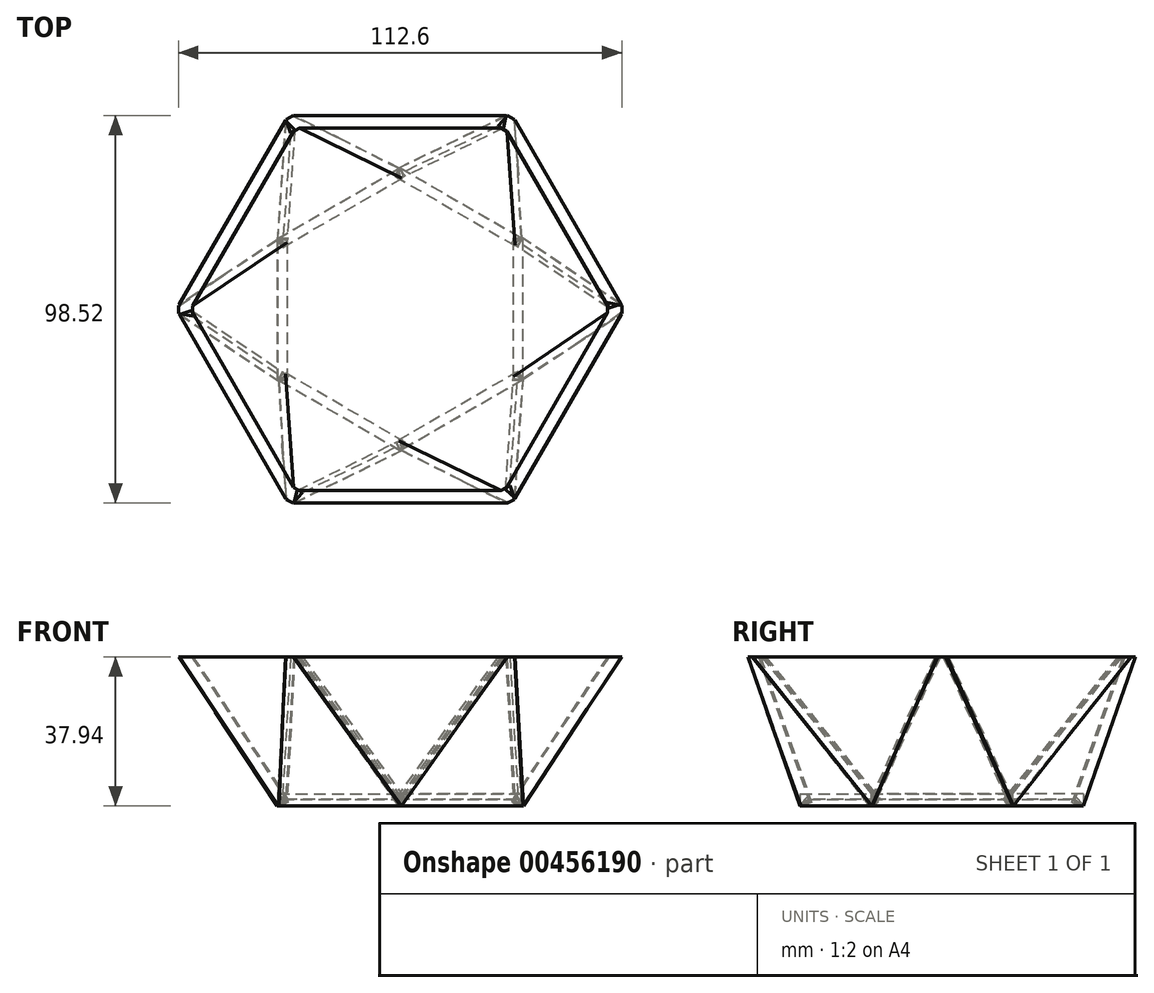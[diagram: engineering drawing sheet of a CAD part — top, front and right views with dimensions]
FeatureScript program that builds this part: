
annotation { "Feature Type Name" : "Feature", "Feature Type Description" : "" }
export const myFeature = defineFeature(function(context is Context, id is Id, definition is map)
    precondition{}
    {
        {
            var Q0;
            Q0=qCreatedBy(makeId("Top.planeOp"),FACE);
            cPlane(context, id + "F0", {"entities" : qUnion([Q0]), "cplaneType" : CPlaneType.OFFSET, "offset" : 40 * mm, "width" : 150 * mm, "height" : 150 * mm});
        }
        {
            var Q0;
            Q0=qCreatedBy(id+"F0.planeOp",FACE);
            var sketch = newSketch(context, id + "F1", { "sketchPlane" : qUnion([Q0])});
            skCircle(sketch, "E0.cCircle", {"center": v(0, 0) * mm, "radius": 50 * mm, "construction": true});
            skLineSegment(sketch, "E0.0", {"start": v(-28.87, 50) * mm, "end": v(28.87, 50) * mm});
            skLineSegment(sketch, "E0.1", {"start": v(28.87, 50) * mm, "end": v(57.74, 0) * mm});
            skLineSegment(sketch, "E0.2", {"start": v(57.74, 0) * mm, "end": v(28.87, -50) * mm});
            skLineSegment(sketch, "E0.3", {"start": v(28.87, -50) * mm, "end": v(-28.87, -50) * mm});
            skLineSegment(sketch, "E0.4", {"start": v(-28.87, -50) * mm, "end": v(-57.74, 0) * mm});
            skLineSegment(sketch, "E0.5", {"start": v(-57.74, 0) * mm, "end": v(-28.87, 50) * mm});
            skPoint(sketch, "E0.0.midPoint", {"position": v(0, 50) * mm});
            skSolve(sketch);
        }
        {
            var Q0;
            Q0=qCreatedBy(makeId("Top.planeOp"),FACE);
            var sketch = newSketch(context, id + "F2", { "sketchPlane" : qUnion([Q0])});
            skCircle(sketch, "E1.cCircle", {"center": v(0, 0) * mm, "radius": 31.13 * mm, "construction": true});
            skLineSegment(sketch, "E1.0", {"start": v(31.13, 17.97) * mm, "end": v(31.13, -17.97) * mm});
            skLineSegment(sketch, "E1.1", {"start": v(31.13, -17.97) * mm, "end": v(0, -35.94) * mm});
            skLineSegment(sketch, "E1.2", {"start": v(0, -35.94) * mm, "end": v(-31.13, -17.97) * mm});
            skLineSegment(sketch, "E1.3", {"start": v(-31.13, -17.97) * mm, "end": v(-31.13, 17.97) * mm});
            skLineSegment(sketch, "E1.4", {"start": v(-31.13, 17.97) * mm, "end": v(0, 35.94) * mm});
            skLineSegment(sketch, "E1.5", {"start": v(0, 35.94) * mm, "end": v(31.13, 17.97) * mm});
            skPoint(sketch, "E1.0.midPoint", {"position": v(31.13, 0) * mm});
            skSolve(sketch);
        }
        {
            var Q0;
            Q0=qCreatedBy(makeId("Right.planeOp"),FACE);
            var sketch = newSketch(context, id + "F3", { "sketchPlane" : qUnion([Q0])});
            skLineSegment(sketch, "E2", {"start": v(0, 0) * mm, "end": v(0, 43.07) * mm, "construction": true});
            skSolve(sketch);
        }
        {
            var Q0;
            Q0=sQuery(id+"F1.wireOp",VERTEX,"E0.2.start");
            var Q1;
            Q1=sQuery(id+"F2.wireOp",VERTEX,"E1.0.start");
            var Q2;
            Q2=sQuery(id+"F2.wireOp",VERTEX,"E1.1.start");
            cPlane(context, id + "F4", {"entities" : qUnion([Q0, Q1, Q2]), "cplaneType" : CPlaneType.THREE_POINT, "offset" : 25 * mm, "width" : 150 * mm, "height" : 150 * mm});
        }
        {
            var Q0;
            Q0=qCreatedBy(id+"F4.planeOp",FACE);
            var sketch = newSketch(context, id + "F5", { "sketchPlane" : qUnion([Q0])});
            skLineSegment(sketch, "E3", {"start": v(0, 65.38) * mm, "end": v(18.06, 17.19) * mm});
            skLineSegment(sketch, "E4", {"start": v(18.06, 17.19) * mm, "end": v(-17.95, 17.19) * mm});
            skLineSegment(sketch, "E5", {"start": v(-17.95, 17.19) * mm, "end": v(0, 65.38) * mm});
            skSolve(sketch);
        }
        {
            var Q0;
            Q0=makeQuery(id+"F5.imprint","IMPRINT",FACE,{"disambiguationData":[TD([[makeQuery(id+"F5.imprint","IMPRINT",EDGE,{"derivedFrom":sQuery(id+"F5.wireOp",EDGE,"E3")}),-1.0]])]});
            extrude(context, id + "F6", {"entities" : qUnion([Q0]), "oppositeDirection" : true, "depth" : 3 * mm});
        }
        {
            var Q0;
            Q0=sQuery(id+"F1.wireOp",VERTEX,"E0.3.start");
            var Q1;
            Q1=sQuery(id+"F1.wireOp",VERTEX,"E0.2.start");
            var Q2;
            Q2=sQuery(id+"F2.wireOp",VERTEX,"E1.1.start");
            cPlane(context, id + "F7", {"entities" : qUnion([Q0, Q1, Q2]), "cplaneType" : CPlaneType.THREE_POINT, "offset" : 25 * mm, "width" : 150 * mm, "height" : 150 * mm});
        }
        {
            var Q0;
            Q0=qCreatedBy(id+"F7.planeOp",FACE);
            var sketch = newSketch(context, id + "F8", { "sketchPlane" : qUnion([Q0])});
            skLineSegment(sketch, "E6", {"start": v(-38.42, 48.23) * mm, "end": v(-1.89, 11.66) * mm});
            skLineSegment(sketch, "E7", {"start": v(-1.89, 11.66) * mm, "end": v(18.24, 59.61) * mm});
            skLineSegment(sketch, "E8", {"start": v(18.24, 59.61) * mm, "end": v(-38.42, 48.23) * mm});
            skSolve(sketch);
        }
        {
            var Q0;
            Q0=makeQuery(id+"F8.imprint","IMPRINT",FACE,{"disambiguationData":[TD([[makeQuery(id+"F8.imprint","IMPRINT",EDGE,{"derivedFrom":sQuery(id+"F8.wireOp",EDGE,"E6")}),1.0]])]});
            extrude(context, id + "F9", {"entities" : qUnion([Q0]), "operationType" : NewBodyOperationType.ADD, "oppositeDirection" : true, "depth" : 3 * mm});
        }
        {
            var Q0;
            Q0=makeQuery(id+"F6.opExtrude","SWEPT_BODY",BODY,{"disambiguationData":[OSD([sQuery(id+"F5.wireOp",EDGE,"E3"),sQuery(id+"F5.wireOp",EDGE,"E4"),sQuery(id+"F5.wireOp",EDGE,"E5")])]});
            var Q1;
            Q1=sQuery(id+"F3.wireOp",EDGE,"E2");
            circularPattern(context, id + "F10", {"entities" : qUnion([Q0]), "axis" : qUnion([Q1]), "angle" : 360 * degree, "instanceCount" : 6, "equalSpace" : true});
        }
        {
            var Q0;
            Q0=makeQuery(id+"F2.imprint","IMPRINT",FACE,{"disambiguationData":[TD([[makeQuery(id+"F2.imprint","IMPRINT",EDGE,{"derivedFrom":sQuery(id+"F2.wireOp",EDGE,"E1.0")}),-1.0]])]});
            extrude(context, id + "F11", {"entities" : qUnion([Q0]), "depth" : 3 * mm});
        }
        {
            var Q0;
            Q0=qCreatedBy(makeId("Right.planeOp"),FACE);
            var sketch = newSketch(context, id + "F12", { "sketchPlane" : qUnion([Q0])});
            skLineSegment(sketch, "E9.bottom", {"start": v(-61.3, 49.46) * mm, "end": v(56.69, 49.46) * mm});
            skLineSegment(sketch, "E9.top", {"start": v(-61.3, 37.84) * mm, "end": v(56.69, 37.84) * mm});
            skLineSegment(sketch, "E9.left", {"start": v(-61.3, 49.46) * mm, "end": v(-61.3, 37.84) * mm});
            skLineSegment(sketch, "E9.right", {"start": v(56.69, 49.46) * mm, "end": v(56.69, 37.84) * mm});
            skSolve(sketch);
        }
        {
            var Q0;
            Q0=makeQuery(id+"F12.imprint","IMPRINT",FACE,{"disambiguationData":[TD([[makeQuery(id+"F12.imprint","IMPRINT",EDGE,{"derivedFrom":sQuery(id+"F12.wireOp",EDGE,"E9.bottom")}),-1.0]])]});
            extrude(context, id + "F13", {"entities" : qUnion([Q0]), "operationType" : NewBodyOperationType.REMOVE, "endBound" : BoundingType.SYMMETRIC, "depth" : 120 * mm});
        }
    });
